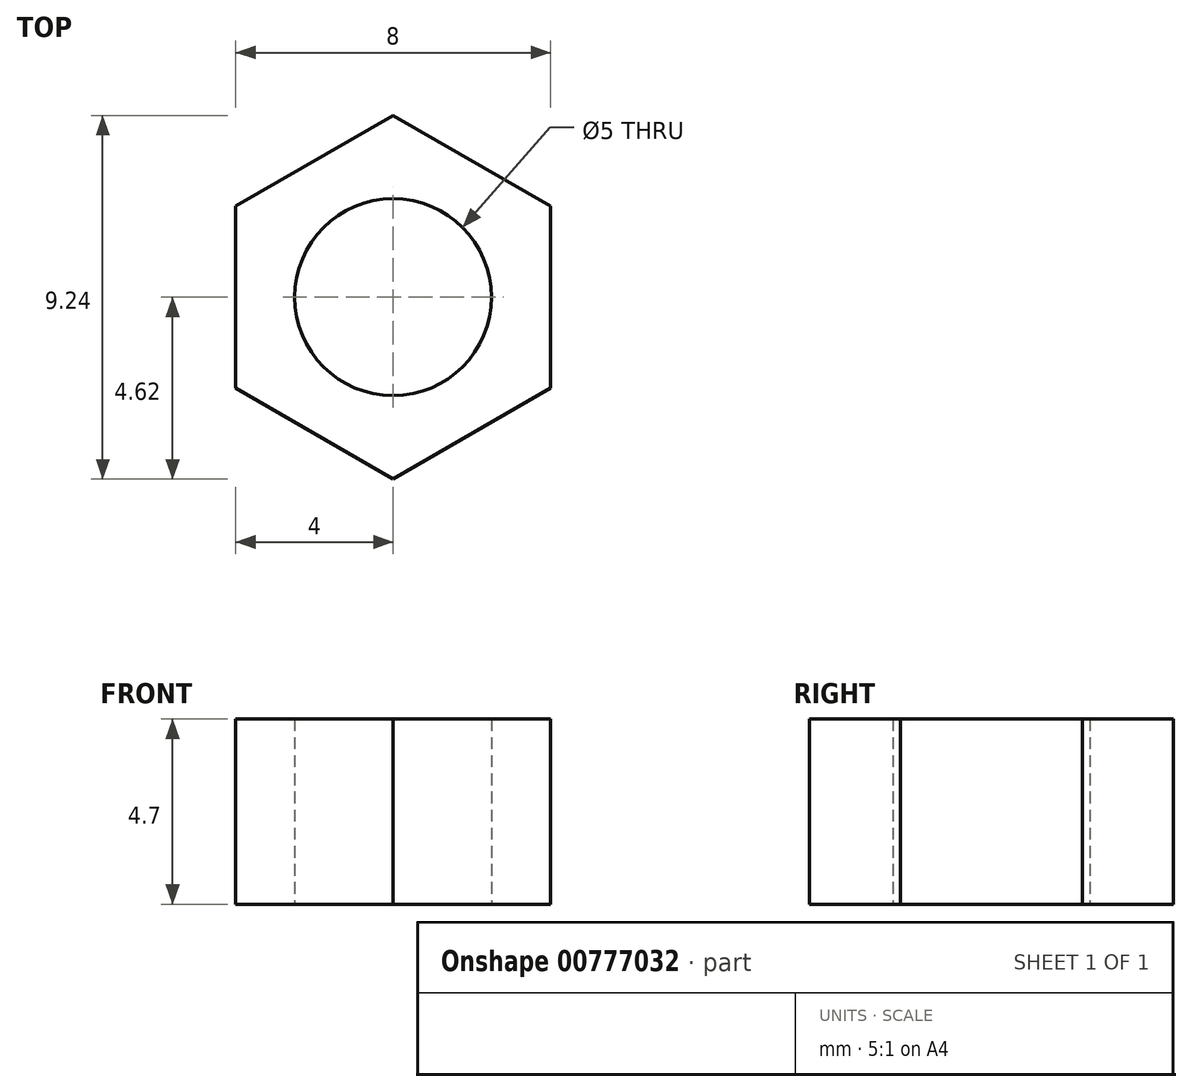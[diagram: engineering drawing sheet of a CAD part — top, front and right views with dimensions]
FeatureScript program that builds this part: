
annotation { "Feature Type Name" : "Feature", "Feature Type Description" : "" }
export const myFeature = defineFeature(function(context is Context, id is Id, definition is map)
    precondition{}
    {
        {
            var Q0;
            Q0=qCreatedBy(makeId("Top.planeOp"),FACE);
            var sketch = newSketch(context, id + "F0", { "sketchPlane" : qUnion([Q0])});
            skCircle(sketch, "E0.cCircle", {"center": v(0, 0) * mm, "radius": 4 * mm, "construction": true});
            skLineSegment(sketch, "E0.0", {"start": v(4, 2.3) * mm, "end": v(4, -2.3) * mm});
            skLineSegment(sketch, "E0.1", {"start": v(4, -2.3) * mm, "end": v(0, -4.62) * mm});
            skLineSegment(sketch, "E0.2", {"start": v(0, -4.62) * mm, "end": v(-4, -2.3) * mm});
            skLineSegment(sketch, "E0.3", {"start": v(-4, -2.3) * mm, "end": v(-4, 2.3) * mm});
            skLineSegment(sketch, "E0.4", {"start": v(-4, 2.3) * mm, "end": v(0, 4.62) * mm});
            skLineSegment(sketch, "E0.5", {"start": v(0, 4.62) * mm, "end": v(4, 2.3) * mm});
            skPoint(sketch, "E0.0.midPoint", {"position": v(4, 0) * mm});
            skCircle(sketch, "E1", {"center": v(0, 0) * mm, "radius": 2.5 * mm});
            skSolve(sketch);
        }
        {
            var Q0;
            Q0=qSketchRegion(id+"F0",true);
            extrude(context, id + "F1", {"entities" : qUnion([Q0]), "depth" : 4.7 * mm, "offsetDistance" : 25 * mm});
        }
    });
